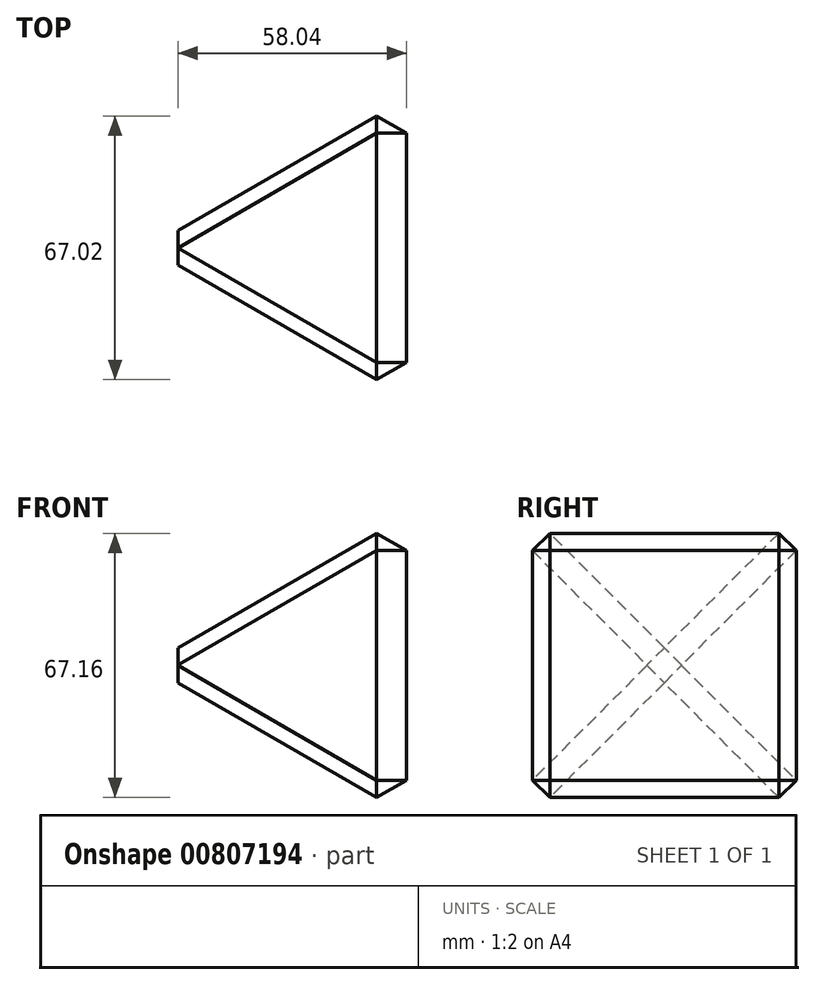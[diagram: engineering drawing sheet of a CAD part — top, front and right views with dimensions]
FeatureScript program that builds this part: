
annotation { "Feature Type Name" : "Feature", "Feature Type Description" : "" }
export const myFeature = defineFeature(function(context is Context, id is Id, definition is map)
    precondition{}
    {
        {
            var Q0;
            Q0=qCreatedBy(makeId("Right.planeOp"),FACE);
            var sketch = newSketch(context, id + "F0", { "sketchPlane" : qUnion([Q0])});
            skLineSegment(sketch, "E0.bottom", {"start": v(75.82, 75.96) * mm, "end": v(0, 75.96) * mm});
            skLineSegment(sketch, "E0.top", {"start": v(75.82, 0) * mm, "end": v(0, 0) * mm});
            skLineSegment(sketch, "E0.left", {"start": v(75.82, 75.96) * mm, "end": v(75.82, 0) * mm});
            skLineSegment(sketch, "E0.right", {"start": v(0, 75.96) * mm, "end": v(0, 0) * mm});
            skSolve(sketch);
        }
        {
            var Q0;
            Q0=makeQuery(id+"F0.imprint","IMPRINT",FACE,{"disambiguationData":[TD([[makeQuery(id+"F0.imprint","IMPRINT",EDGE,{"derivedFrom":sQuery(id+"F0.wireOp",EDGE,"E0.bottom")}),1.0]])]});
            extrude(context, id + "F1", {"entities" : qUnion([Q0]), "oppositeDirection" : true, "depth" : 68.33 * mm, "offsetDistance" : 25.4 * mm, "hasDraft" : true, "draftAngle" : 30 * degree, "draftPullDirection" : true});
        }
        {
            var Q0;
            Q0=makeQuery(id+"F1.opExtrude","SWEPT_FACE",FACE,{"disambiguationData":[OSD([sQuery(id+"F0.wireOp",EDGE,"E0.right")])]});
            var Q1;
            Q1=makeQuery(id+"F1.opExtrude","SWEPT_FACE",FACE,{"disambiguationData":[OSD([sQuery(id+"F0.wireOp",EDGE,"E0.bottom")])]});
            var Q2;
            Q2=makeQuery(id+"F1.opExtrude","SWEPT_FACE",FACE,{"disambiguationData":[OSD([sQuery(id+"F0.wireOp",EDGE,"E0.left")])]});
            var Q3;
            Q3=makeQuery(id+"F1.opExtrude","SWEPT_FACE",FACE,{"disambiguationData":[OSD([sQuery(id+"F0.wireOp",EDGE,"E0.top")])]});
            chamfer(context, id + "F2", {"entities" : qUnion([Q0, Q1, Q2, Q3]), "width" : 5.08 * mm, "tangentPropagation" : true});
        }
    });
